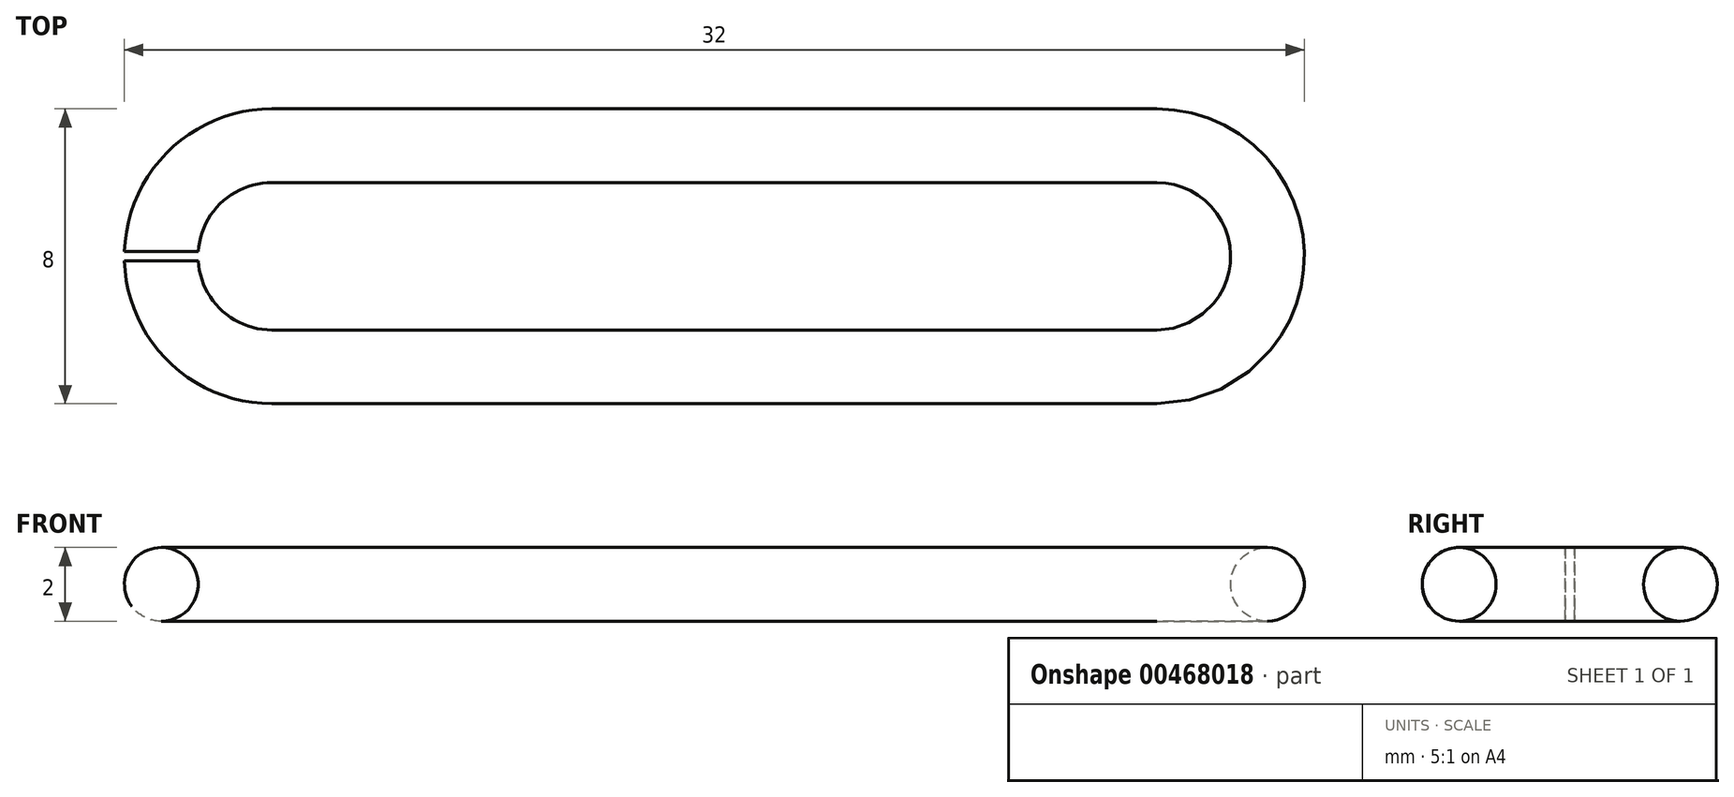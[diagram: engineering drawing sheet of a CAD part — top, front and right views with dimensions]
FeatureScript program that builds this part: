
annotation { "Feature Type Name" : "Feature", "Feature Type Description" : "" }
export const myFeature = defineFeature(function(context is Context, id is Id, definition is map)
    precondition{}
    {
        {
            var Q0;
            Q0=qCreatedBy(makeId("Top.planeOp"),FACE);
            var sketch = newSketch(context, id + "F0", { "sketchPlane" : qUnion([Q0])});
            skLineSegment(sketch, "E0.bottom", {"start": v(14, -2) * mm, "end": v(-14, -2) * mm});
            skLineSegment(sketch, "E0.top", {"start": v(14, 2) * mm, "end": v(-14, 2) * mm});
            skLineSegment(sketch, "E0.left", {"start": v(14, -2) * mm, "end": v(14, 2) * mm});
            skLineSegment(sketch, "E0.right", {"start": v(-14, -2) * mm, "end": v(-14, 2) * mm});
            skPoint(sketch, "E0.middle", {"position": v(0, 0) * mm});
            skLineSegment(sketch, "E1.bottom", {"start": v(16, -4) * mm, "end": v(-16, -4) * mm});
            skLineSegment(sketch, "E1.top", {"start": v(16, 4) * mm, "end": v(-16, 4) * mm});
            skLineSegment(sketch, "E1.left", {"start": v(16, -4) * mm, "end": v(16, 4) * mm});
            skLineSegment(sketch, "E1.right", {"start": v(-16, -4) * mm, "end": v(-16, 4) * mm});
            skSolve(sketch);
        }
        {
            var Q0;
            Q0=makeQuery(id+"F0.imprint","IMPRINT",FACE,{"disambiguationData":[TD([[makeQuery(id+"F0.imprint","IMPRINT",EDGE,{"derivedFrom":sQuery(id+"F0.wireOp",EDGE,"E0.bottom")}),1.0]])]});
            extrude(context, id + "F1", {"entities" : qUnion([Q0]), "depth" : 2 * mm, "offsetDistance" : 25 * mm});
        }
        {
            var Q0;
            Q0=makeQuery(id+"F1.opExtrude","SWEPT_EDGE",EDGE,{"disambiguationData":[OSD([sQuery(id+"F0.wireOp",EDGE,"E0.top"),sQuery(id+"F0.wireOp",EDGE,"E0.right")])]});
            var Q1;
            Q1=makeQuery(id+"F1.opExtrude","SWEPT_EDGE",EDGE,{"disambiguationData":[OSD([sQuery(id+"F0.wireOp",EDGE,"E0.bottom"),sQuery(id+"F0.wireOp",EDGE,"E0.right")])]});
            var Q2;
            Q2=makeQuery(id+"F1.opExtrude","SWEPT_EDGE",EDGE,{"disambiguationData":[OSD([sQuery(id+"F0.wireOp",EDGE,"E0.top"),sQuery(id+"F0.wireOp",EDGE,"E0.left")])]});
            var Q3;
            Q3=makeQuery(id+"F1.opExtrude","SWEPT_EDGE",EDGE,{"disambiguationData":[OSD([sQuery(id+"F0.wireOp",EDGE,"E0.bottom"),sQuery(id+"F0.wireOp",EDGE,"E0.left")])]});
            fillet(context, id + "F2", {"entities" : qUnion([Q0, Q1, Q2, Q3]), "radius" : 2 * mm, "tangentPropagation" : true, "allowEdgeOverflow" : false});
        }
        {
            var Q0;
            Q0=makeQuery(id+"F1.opExtrude","SWEPT_EDGE",EDGE,{"disambiguationData":[OSD([sQuery(id+"F0.wireOp",EDGE,"E1.top"),sQuery(id+"F0.wireOp",EDGE,"E1.right")])]});
            var Q1;
            Q1=makeQuery(id+"F1.opExtrude","SWEPT_EDGE",EDGE,{"disambiguationData":[OSD([sQuery(id+"F0.wireOp",EDGE,"E1.top"),sQuery(id+"F0.wireOp",EDGE,"E1.left")])]});
            var Q2;
            Q2=makeQuery(id+"F1.opExtrude","SWEPT_EDGE",EDGE,{"disambiguationData":[OSD([sQuery(id+"F0.wireOp",EDGE,"E1.bottom"),sQuery(id+"F0.wireOp",EDGE,"E1.left")])]});
            var Q3;
            Q3=makeQuery(id+"F1.opExtrude","SWEPT_EDGE",EDGE,{"disambiguationData":[OSD([sQuery(id+"F0.wireOp",EDGE,"E1.bottom"),sQuery(id+"F0.wireOp",EDGE,"E1.right")])]});
            fillet(context, id + "F3", {"entities" : qUnion([Q0, Q1, Q2, Q3]), "radius" : 4 * mm, "tangentPropagation" : true, "allowEdgeOverflow" : false});
        }
        {
            var Q0;
            Q0=makeQuery(id+"F1.opExtrude","CAP_EDGE",EDGE,{"disambiguationData":[OSD([sQuery(id+"F0.wireOp",EDGE,"E1.top")])],"isStart":false});
            var Q1;
            Q1=makeQuery(id+"F1.opExtrude","CAP_EDGE",EDGE,{"disambiguationData":[OSD([sQuery(id+"F0.wireOp",EDGE,"E0.top")])],"isStart":false});
            var Q2;
            Q2=makeQuery(id+"F1.opExtrude","CAP_EDGE",EDGE,{"disambiguationData":[OSD([sQuery(id+"F0.wireOp",EDGE,"E0.top")])],"isStart":true});
            var Q3;
            Q3=makeQuery(id+"F1.opExtrude","CAP_EDGE",EDGE,{"disambiguationData":[OSD([sQuery(id+"F0.wireOp",EDGE,"E1.top")])],"isStart":true});
            fillet(context, id + "F4", {"entities" : qUnion([Q0, Q1, Q2, Q3]), "radius" : 1 * mm, "tangentPropagation" : true, "allowEdgeOverflow" : false});
        }
        {
            var Q0;
            Q0=qCreatedBy(makeId("Top.planeOp"),FACE);
            var sketch = newSketch(context, id + "F5", { "sketchPlane" : qUnion([Q0])});
            skLineSegment(sketch, "E2.bottom", {"start": v(-13.42, -0.12) * mm, "end": v(-16.42, -0.12) * mm});
            skLineSegment(sketch, "E2.top", {"start": v(-13.42, 0.13) * mm, "end": v(-16.42, 0.13) * mm});
            skLineSegment(sketch, "E2.left", {"start": v(-13.42, -0.12) * mm, "end": v(-13.42, 0.13) * mm});
            skLineSegment(sketch, "E2.right", {"start": v(-16.42, -0.12) * mm, "end": v(-16.42, 0.13) * mm});
            skPoint(sketch, "E2.middle", {"position": v(-14.92, 0) * mm});
            skSolve(sketch);
        }
        {
            var Q0;
            Q0=makeQuery(id+"F5.imprint","IMPRINT",FACE,{"disambiguationData":[TD([[makeQuery(id+"F5.imprint","IMPRINT",EDGE,{"derivedFrom":sQuery(id+"F5.wireOp",EDGE,"E2.bottom")}),-1.0]])]});
            extrude(context, id + "F6", {"entities" : qUnion([Q0]), "operationType" : NewBodyOperationType.REMOVE, "depth" : 25 * mm, "offsetDistance" : 25 * mm});
        }
    });
